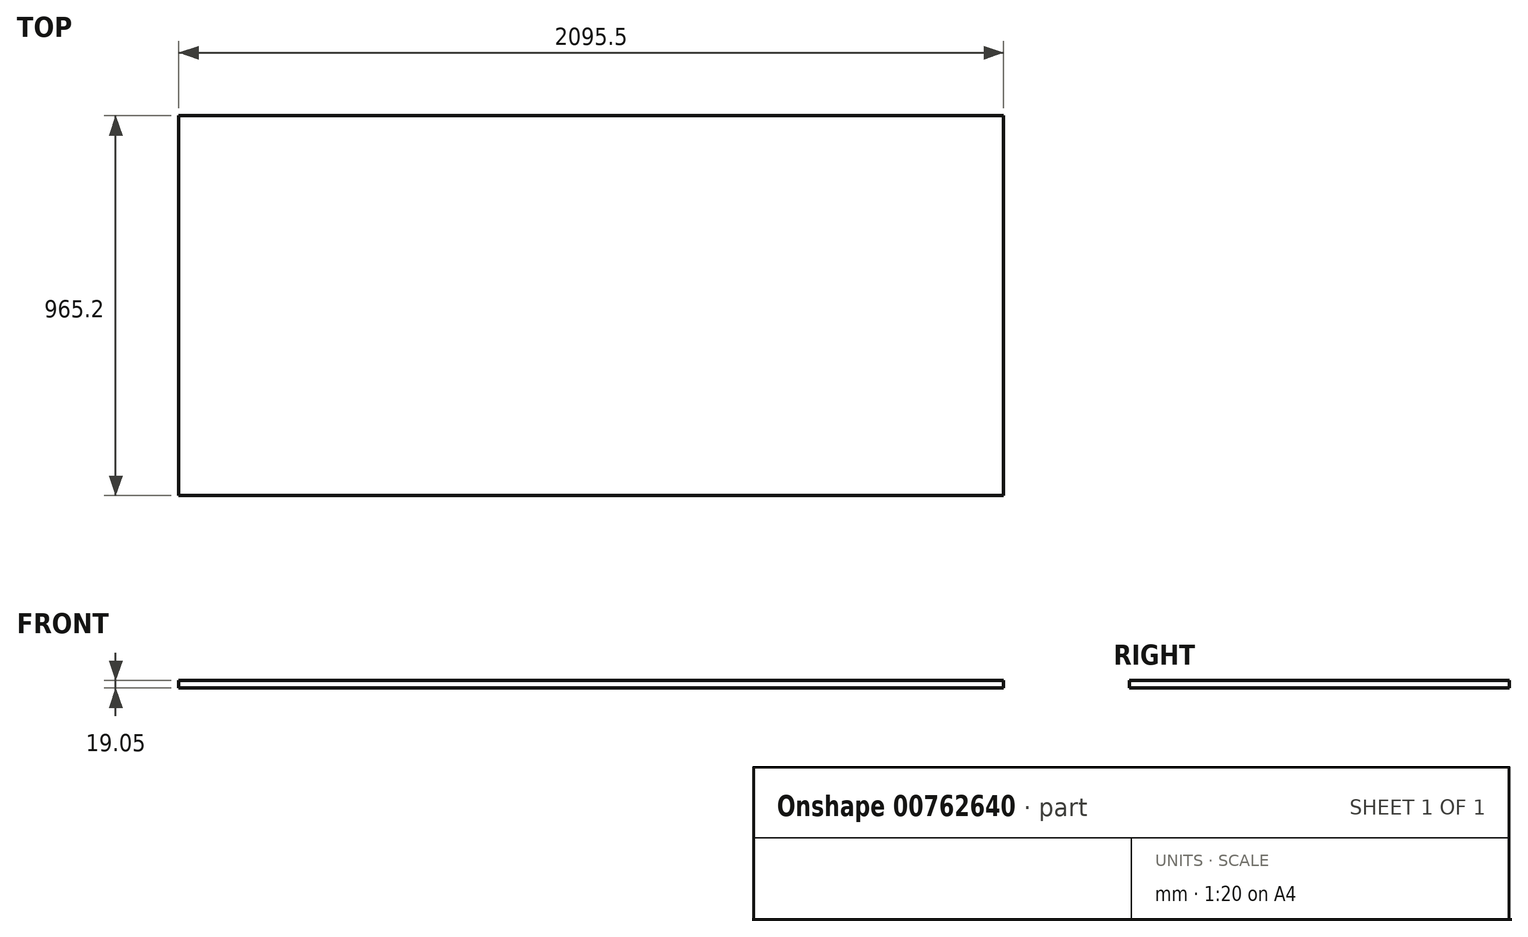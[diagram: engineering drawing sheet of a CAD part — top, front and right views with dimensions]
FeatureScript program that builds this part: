
annotation { "Feature Type Name" : "Feature", "Feature Type Description" : "" }
export const myFeature = defineFeature(function(context is Context, id is Id, definition is map)
    precondition{}
    {
        {
            var Q0;
            Q0=qCreatedBy(makeId("Top.planeOp"),FACE);
            var sketch = newSketch(context, id + "F0", { "sketchPlane" : qUnion([Q0])});
            skLineSegment(sketch, "E0.bottom", {"start": v(-1047.75, 482.6) * mm, "end": v(1047.75, 482.6) * mm});
            skLineSegment(sketch, "E0.top", {"start": v(-1047.75, -482.6) * mm, "end": v(1047.75, -482.6) * mm});
            skLineSegment(sketch, "E0.left", {"start": v(-1047.75, 482.6) * mm, "end": v(-1047.75, -482.6) * mm});
            skLineSegment(sketch, "E0.right", {"start": v(1047.75, 482.6) * mm, "end": v(1047.75, -482.6) * mm});
            skPoint(sketch, "E0.middle", {"position": v(0, 0) * mm});
            skSolve(sketch);
        }
        {
            var Q0;
            Q0=makeQuery(id+"F0.imprint","IMPRINT",FACE,{"disambiguationData":[TD([[makeQuery(id+"F0.imprint","IMPRINT",EDGE,{"derivedFrom":sQuery(id+"F0.wireOp",EDGE,"E0.bottom")}),-1.0]])]});
            extrude(context, id + "F1", {"entities" : qUnion([Q0]), "depth" : 19.05 * mm, "offsetDistance" : 25.4 * mm});
        }
    });
